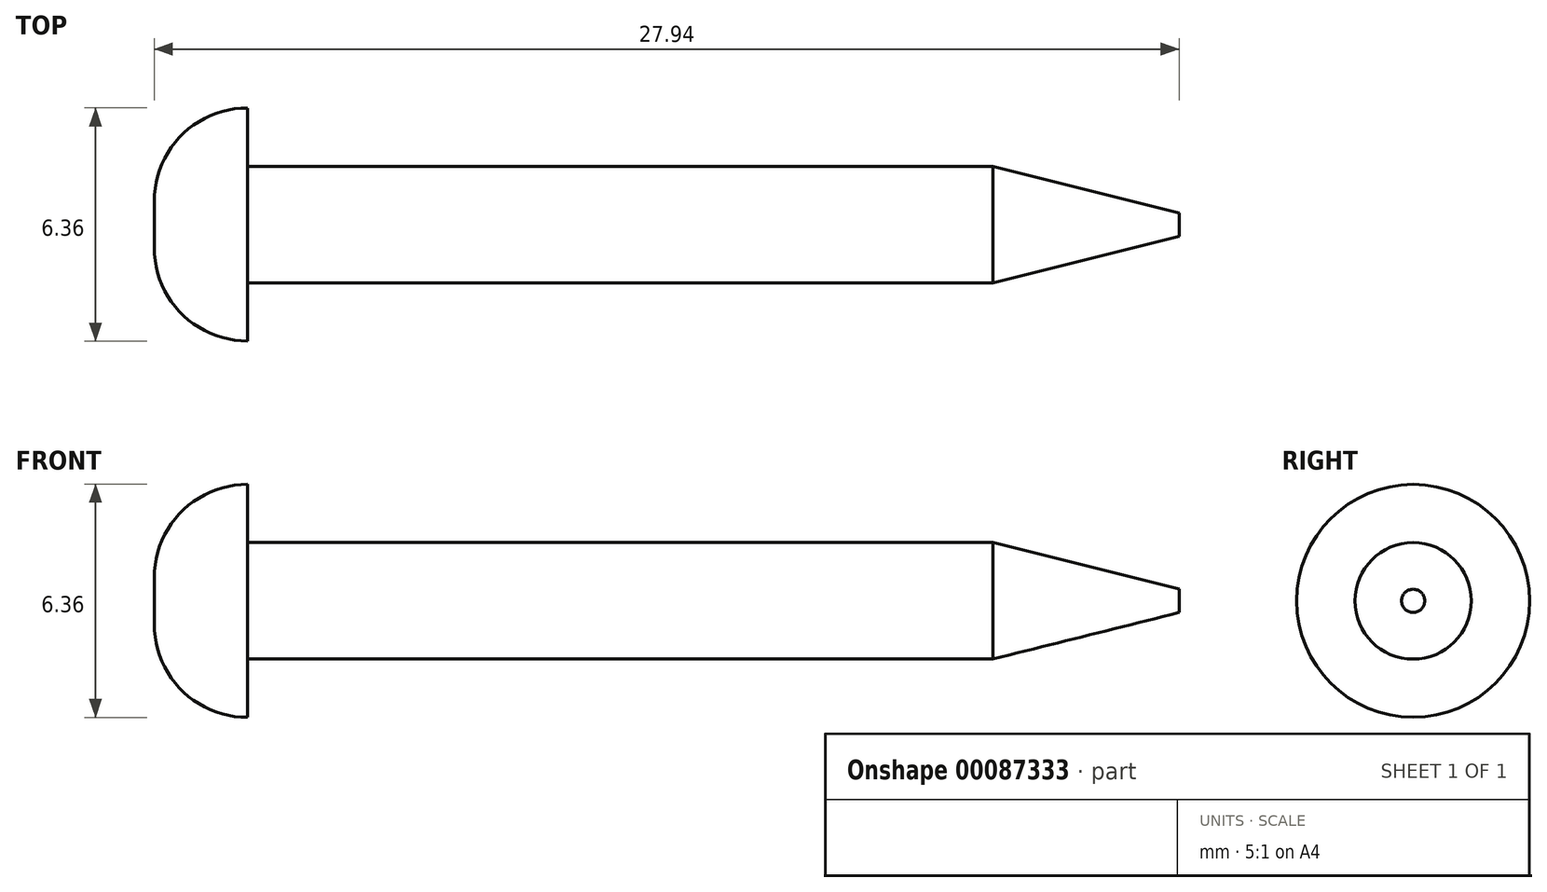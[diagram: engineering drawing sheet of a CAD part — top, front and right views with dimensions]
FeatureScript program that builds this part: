
annotation { "Feature Type Name" : "Feature", "Feature Type Description" : "" }
export const myFeature = defineFeature(function(context is Context, id is Id, definition is map)
    precondition{}
    {
        {
            var Q0;
            Q0=qCreatedBy(makeId("Right.planeOp"),FACE);
            var sketch = newSketch(context, id + "F0", { "sketchPlane" : qUnion([Q0])});
            skCircle(sketch, "E0", {"center": v(0, 0) * mm, "radius": 1.59 * mm});
            skSolve(sketch);
        }
        {
            var Q0;
            Q0=qSketchRegion(id+"F0",true);
            extrude(context, id + "F1", {"entities" : qUnion([Q0]), "oppositeDirection" : true, "depth" : 25.4 * mm});
        }
        {
            var Q0;
            Q0=makeQuery(id+"F1.opExtrude","CAP_FACE",FACE,{"disambiguationData":[OSD([sQuery(id+"F0.wireOp",EDGE,"E0")])],"isStart":false});
            var sketch = newSketch(context, id + "F2", { "sketchPlane" : qUnion([Q0])});
            skCircle(sketch, "E1", {"center": v(0, 0) * mm, "radius": 3.17 * mm});
            skSolve(sketch);
        }
        {
            var Q0;
            Q0=makeQuery(id+"F2.imprint","IMPRINT",FACE,{"disambiguationData":[TD([[makeQuery(id+"F2.imprint","IMPRINT",EDGE,{"derivedFrom":sQuery(id+"F2.wireOp",EDGE,"E1")}),1.0]])]});
            var Q1;
            Q1=makeQuery(id+"F2.imprint","IMPRINT",FACE,{"disambiguationData":[TD([[makeQuery(id+"F2.imprint","IMPRINT",EDGE,{"derivedFrom":makeQuery(id+"F1.opExtrude","CAP_EDGE",EDGE,{"disambiguationData":[OSD([sQuery(id+"F0.wireOp",EDGE,"E0")])],"isStart":false})}),-1.0]])]});
            extrude(context, id + "F3", {"entities" : qUnion([Q0, Q1]), "operationType" : NewBodyOperationType.ADD, "depth" : 2.54 * mm});
        }
        {
            var Q0;
            Q0=makeQuery(id+"F3.opExtrude","CAP_EDGE",EDGE,{"disambiguationData":[OSD([sQuery(id+"F2.wireOp",EDGE,"E1")])],"isStart":false});
            fillet(context, id + "F4", {"entities" : qUnion([Q0]), "radius" : 2.54 * mm, "tangentPropagation" : true, "allowEdgeOverflow" : false});
        }
        {
            var Q0;
            Q0=makeQuery(id+"F1.opExtrude","CAP_EDGE",EDGE,{"disambiguationData":[OSD([sQuery(id+"F0.wireOp",EDGE,"E0")])],"isStart":true});
            chamfer(context, id + "F5", {"entities" : qUnion([Q0]), "chamferType" : ChamferType.TWO_OFFSETS, "width1" : 1.27 * mm, "oppositeDirection" : false, "width2" : 5.08 * mm, "tangentPropagation" : true});
        }
    });
